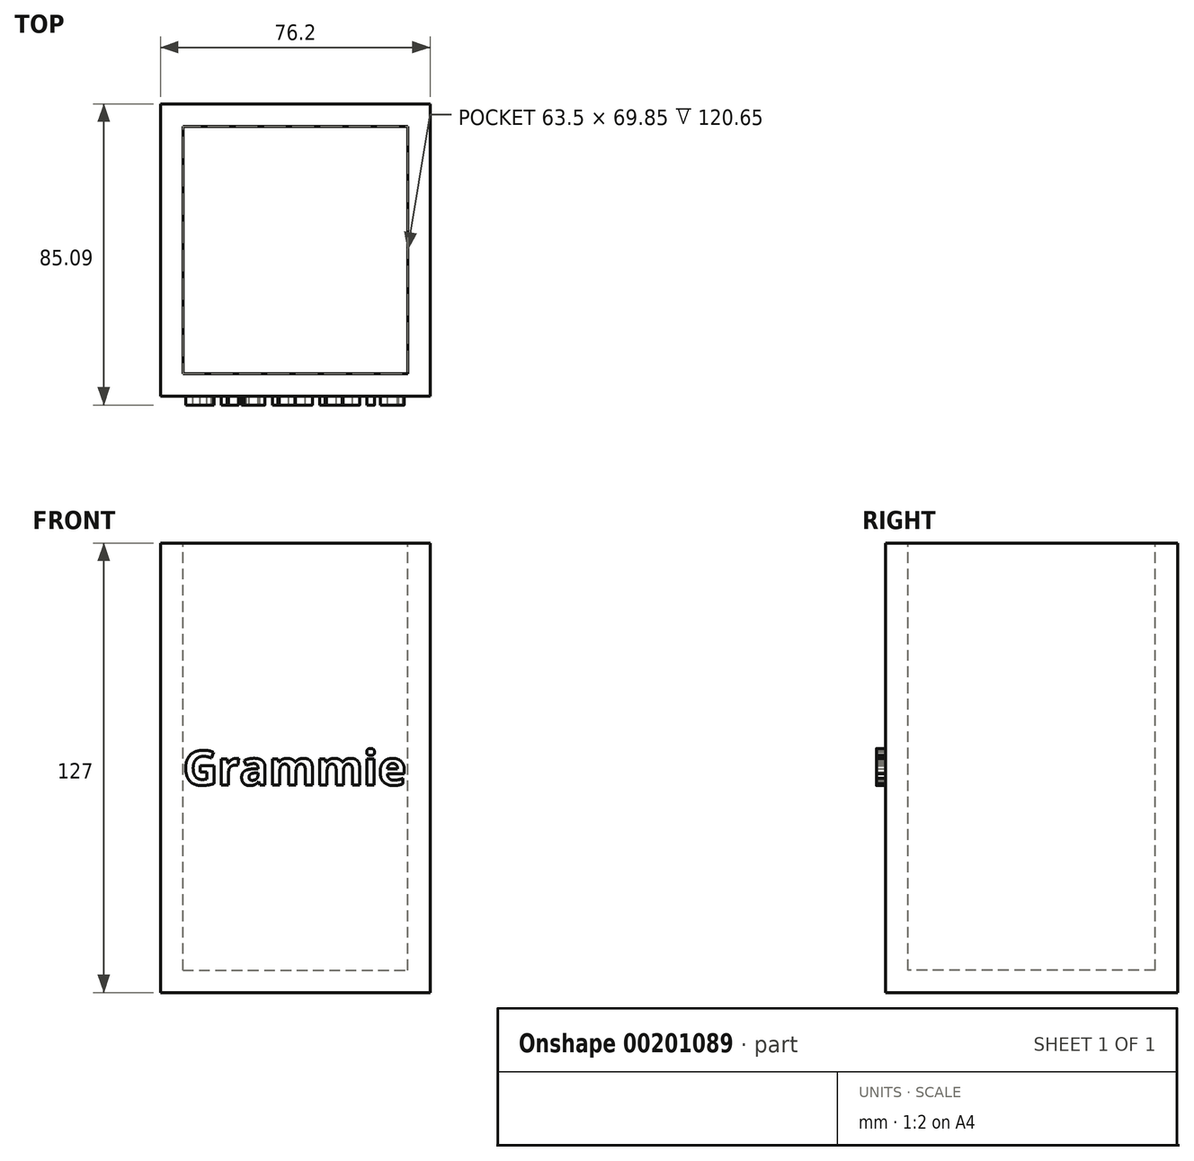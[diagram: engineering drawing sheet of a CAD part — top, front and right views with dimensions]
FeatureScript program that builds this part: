
annotation { "Feature Type Name" : "Feature", "Feature Type Description" : "" }
export const myFeature = defineFeature(function(context is Context, id is Id, definition is map)
    precondition{}
    {
        {
            var Q0;
            Q0=qCreatedBy(makeId("Front.planeOp"),FACE);
            var sketch = newSketch(context, id + "F0", { "sketchPlane" : qUnion([Q0])});
            skLineSegment(sketch, "E0.bottom", {"start": v(-41.79, 58.05) * mm, "end": v(34.41, 58.05) * mm});
            skLineSegment(sketch, "E0.top", {"start": v(-41.79, -68.95) * mm, "end": v(34.41, -68.95) * mm});
            skLineSegment(sketch, "E0.left", {"start": v(-41.79, 58.05) * mm, "end": v(-41.79, -68.95) * mm});
            skLineSegment(sketch, "E0.right", {"start": v(34.41, 58.05) * mm, "end": v(34.41, -68.95) * mm});
            skSolve(sketch);
        }
        {
            var Q0;
            Q0 = qSketchRegion(id + "F0", true);
            extrude(context, id + "F1", {"entities" : qUnion([Q0]), "depth" : 82.55 * mm});
        }
        {
            var Q0;
            Q0=makeQuery(id+"F1.opExtrude","SWEPT_FACE",FACE,{"disambiguationData":[OSD([sQuery(id+"F0.wireOp",EDGE,"E0.bottom")])]});
            var sketch = newSketch(context, id + "F2", { "sketchPlane" : qUnion([Q0])});
            skLineSegment(sketch, "E1.bottom", {"start": v(-35.44, -6.35) * mm, "end": v(28.06, -6.35) * mm});
            skLineSegment(sketch, "E1.top", {"start": v(-35.44, -76.2) * mm, "end": v(28.06, -76.2) * mm});
            skLineSegment(sketch, "E1.left", {"start": v(-35.44, -6.35) * mm, "end": v(-35.44, -76.2) * mm});
            skLineSegment(sketch, "E1.right", {"start": v(28.06, -6.35) * mm, "end": v(28.06, -76.2) * mm});
            skSolve(sketch);
        }
        {
            var Q0;
            Q0 = qSketchRegion(id + "F2", true);
            extrude(context, id + "F3", {"entities" : qUnion([Q0]), "operationType" : NewBodyOperationType.REMOVE, "oppositeDirection" : true, "depth" : 120.65 * mm});
        }
        {
            var Q0;
            Q0=makeQuery(id+"F1.opExtrude","CAP_FACE",FACE,{"disambiguationData":[OSD([sQuery(id+"F0.wireOp",EDGE,"E0.bottom"),sQuery(id+"F0.wireOp",EDGE,"E0.top"),sQuery(id+"F0.wireOp",EDGE,"E0.left"),sQuery(id+"F0.wireOp",EDGE,"E0.right")])],"isStart":false});
            var sketch = newSketch(context, id + "F4", { "sketchPlane" : qUnion([Q0])});
            skText(sketch, "E2", { "text": "Grammie", "fontName": "OpenSans-Bold.ttf"});
            const initialGuessF4  = {"E2": [-0.03544, -0.01035, 1, 0, 0.0098]};
            skSetInitialGuess(sketch, initialGuessF4);
            skSolve(sketch);
        }
        {
            var Q0;
            Q0 = qSketchRegion(id + "F4", true);
            extrude(context, id + "F5", {"entities" : qUnion([Q0]), "operationType" : NewBodyOperationType.ADD, "depth" : 2.54 * mm});
        }
    });
